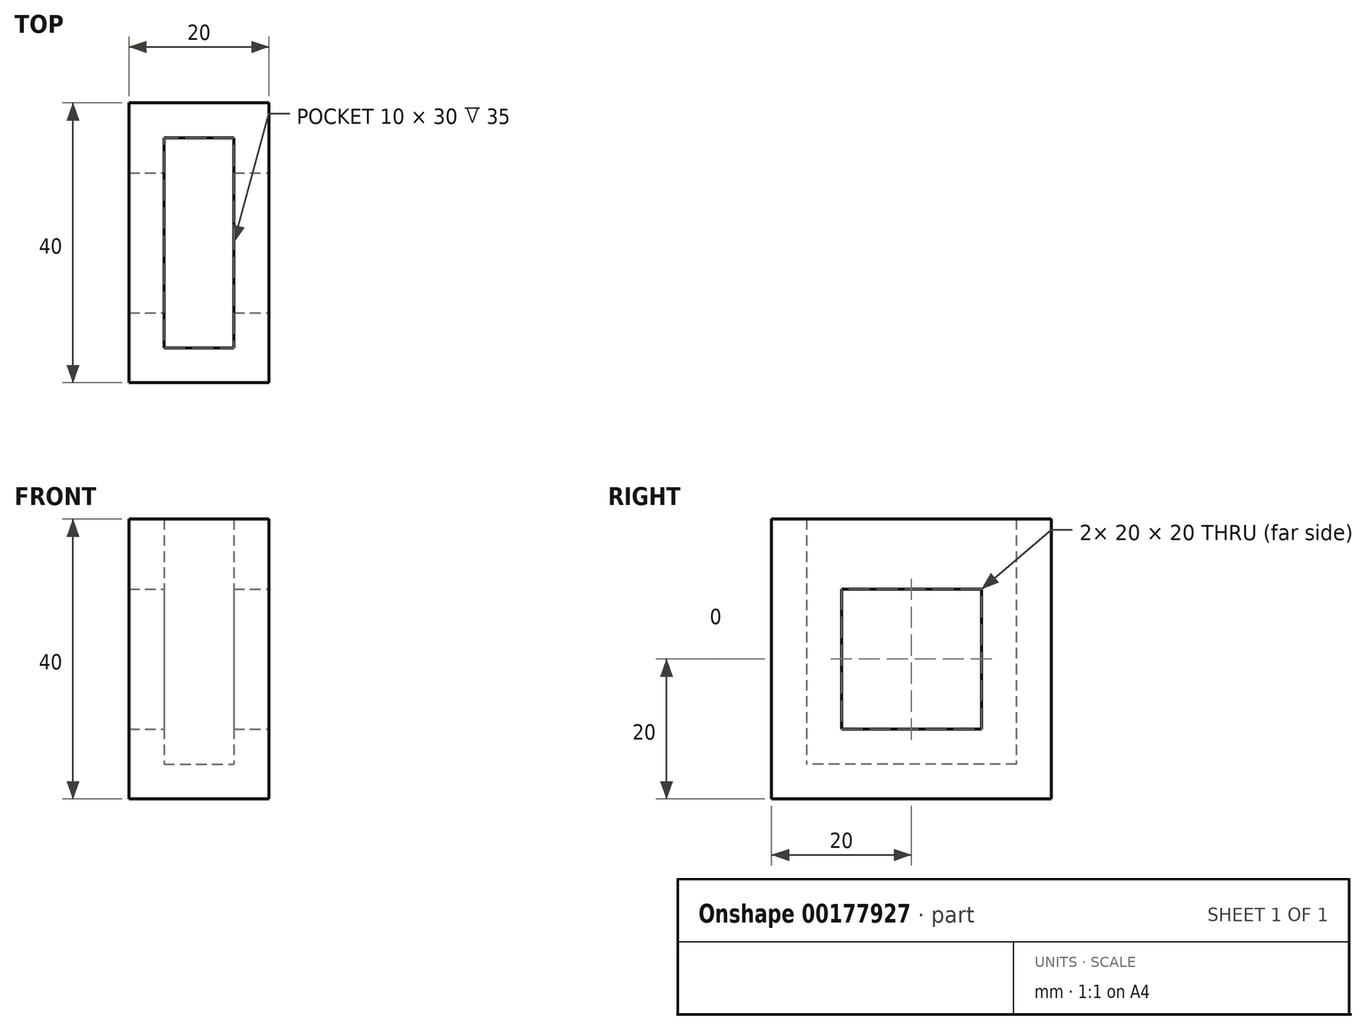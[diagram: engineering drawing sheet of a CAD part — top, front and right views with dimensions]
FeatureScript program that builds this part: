
annotation { "Feature Type Name" : "Feature", "Feature Type Description" : "" }
export const myFeature = defineFeature(function(context is Context, id is Id, definition is map)
    precondition{}
    {
        {
            var Q0;
            Q0=qCreatedBy(makeId("Top.planeOp"),FACE);
            var sketch = newSketch(context, id + "F0", { "sketchPlane" : qUnion([Q0])});
            skLineSegment(sketch, "E0.bottom", {"start": v(-5, 15) * mm, "end": v(5, 15) * mm});
            skLineSegment(sketch, "E0.top", {"start": v(-5, -15) * mm, "end": v(5, -15) * mm});
            skLineSegment(sketch, "E0.left", {"start": v(-5, 15) * mm, "end": v(-5, -15) * mm});
            skLineSegment(sketch, "E0.right", {"start": v(5, 15) * mm, "end": v(5, -15) * mm});
            skPoint(sketch, "E0.middle", {"position": v(0, 0) * mm});
            skLineSegment(sketch, "E1.bottom", {"start": v(-10, 20) * mm, "end": v(10, 20) * mm});
            skLineSegment(sketch, "E1.top", {"start": v(-10, -20) * mm, "end": v(10, -20) * mm});
            skLineSegment(sketch, "E1.left", {"start": v(-10, 20) * mm, "end": v(-10, -20) * mm});
            skLineSegment(sketch, "E1.right", {"start": v(10, 20) * mm, "end": v(10, -20) * mm});
            skSolve(sketch);
        }
        {
            var Q0;
            Q0=makeQuery(id+"F0.imprint","IMPRINT",FACE,{"disambiguationData":[TD([[makeQuery(id+"F0.imprint","IMPRINT",EDGE,{"derivedFrom":sQuery(id+"F0.wireOp",EDGE,"E0.bottom")}),1.0]])]});
            extrude(context, id + "F1", {"entities" : qUnion([Q0]), "depth" : 40 * mm, "offsetDistance" : 25 * mm});
        }
        {
            var Q0;
            Q0=makeQuery(id+"F0.imprint","IMPRINT",FACE,{"disambiguationData":[TD([[makeQuery(id+"F0.imprint","IMPRINT",EDGE,{"derivedFrom":sQuery(id+"F0.wireOp",EDGE,"E0.bottom")}),-1.0]])]});
            extrude(context, id + "F2", {"entities" : qUnion([Q0]), "operationType" : NewBodyOperationType.ADD, "depth" : 5 * mm});
        }
        {
            var Q0;
            Q0=makeQuery(id+"F1.opExtrude","SWEPT_FACE",FACE,{"disambiguationData":[OSD([sQuery(id+"F0.wireOp",EDGE,"E1.right")])]});
            var sketch = newSketch(context, id + "F3", { "sketchPlane" : qUnion([Q0])});
            skLineSegment(sketch, "E2", {"start": v(0, 0) * mm, "end": v(0, 20) * mm});
            skLineSegment(sketch, "E3.bottom", {"start": v(-10, 30) * mm, "end": v(10, 30) * mm});
            skLineSegment(sketch, "E3.top", {"start": v(-10, 10) * mm, "end": v(10, 10) * mm});
            skLineSegment(sketch, "E3.left", {"start": v(-10, 30) * mm, "end": v(-10, 10) * mm});
            skLineSegment(sketch, "E3.right", {"start": v(10, 30) * mm, "end": v(10, 10) * mm});
            skPoint(sketch, "E3.middle", {"position": v(0, 20) * mm});
            skSolve(sketch);
        }
        {
            var Q0;
            Q0=makeQuery(id+"F3.imprint","IMPRINT",FACE,{"disambiguationData":[TD([[makeQuery(id+"F3.imprint","IMPRINT",EDGE,{"derivedFrom":sQuery(id+"F3.wireOp",EDGE,"E3.bottom")}),-1.0]])]});
            extrude(context, id + "F4", {"entities" : qUnion([Q0]), "operationType" : NewBodyOperationType.REMOVE, "oppositeDirection" : true, "depth" : 60 * mm});
        }
    });
